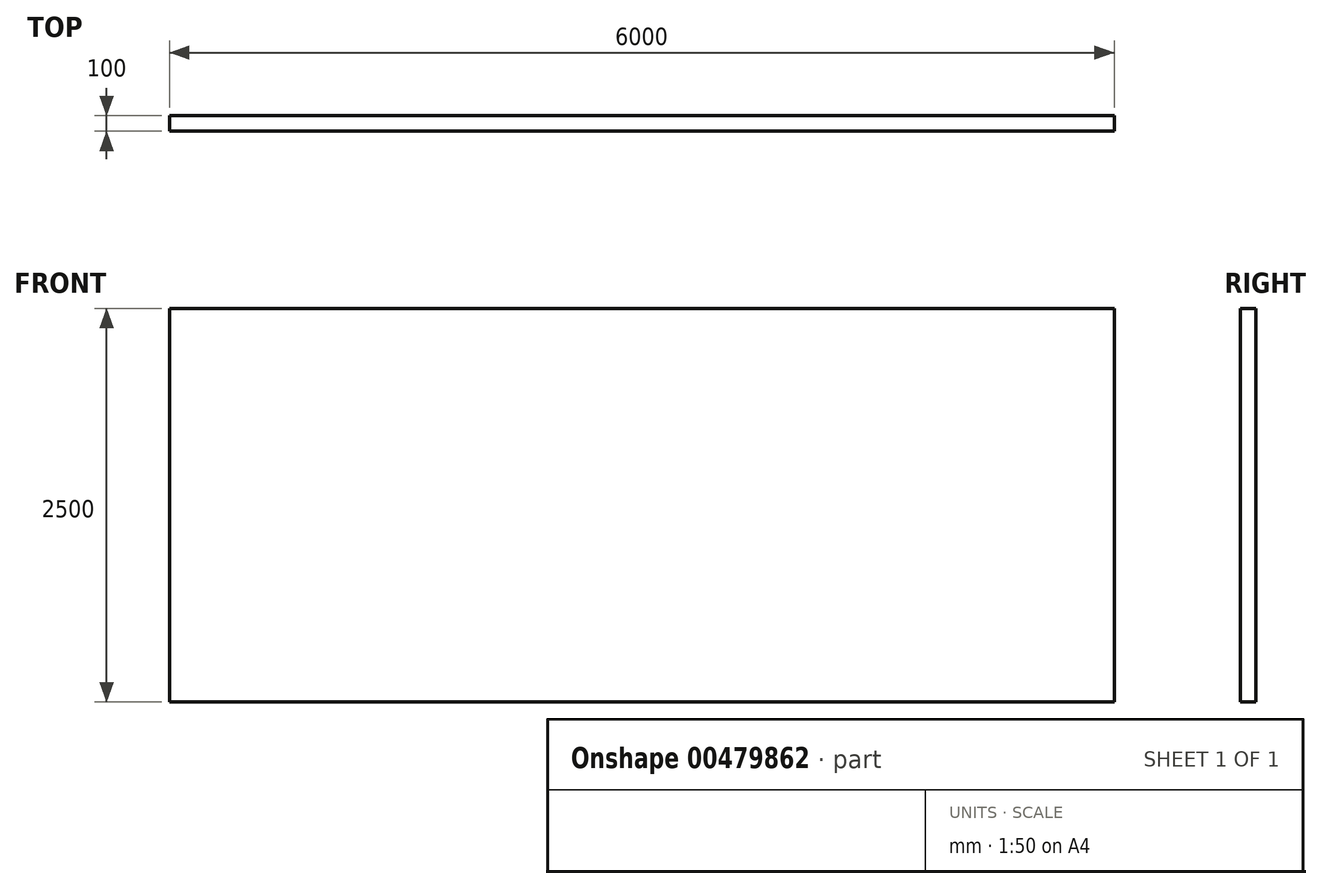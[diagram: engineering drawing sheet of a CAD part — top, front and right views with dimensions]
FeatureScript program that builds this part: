
annotation { "Feature Type Name" : "Feature", "Feature Type Description" : "" }
export const myFeature = defineFeature(function(context is Context, id is Id, definition is map)
    precondition{}
    {
        {
            var Q0;
            Q0=qCreatedBy(makeId("Front.planeOp"),FACE);
            var sketch = newSketch(context, id + "F0", { "sketchPlane" : qUnion([Q0])});
            skLineSegment(sketch, "E0.bottom", {"start": v(2716.87, 0) * mm, "end": v(-3283.13, 0) * mm});
            skLineSegment(sketch, "E0.top", {"start": v(2716.87, 2500) * mm, "end": v(-3283.13, 2500) * mm});
            skLineSegment(sketch, "E0.left", {"start": v(2716.87, 0) * mm, "end": v(2716.87, 2500) * mm});
            skLineSegment(sketch, "E0.right", {"start": v(-3283.13, 0) * mm, "end": v(-3283.13, 2500) * mm});
            skSolve(sketch);
        }
        {
            var Q0;
            Q0=makeQuery(id+"F0.imprint","IMPRINT",FACE,{"disambiguationData":[TD([[makeQuery(id+"F0.imprint","IMPRINT",EDGE,{"derivedFrom":sQuery(id+"F0.wireOp",EDGE,"E0.bottom")}),-1.0]])]});
            extrude(context, id + "F1", {"entities" : qUnion([Q0]), "oppositeDirection" : true, "depth" : 100 * mm});
        }
    });
